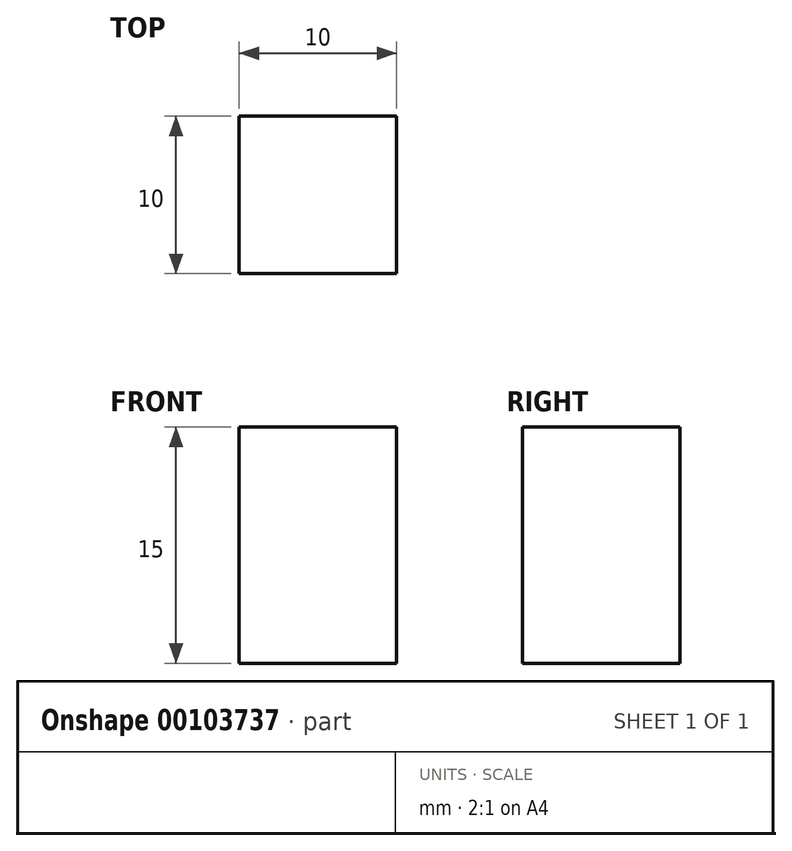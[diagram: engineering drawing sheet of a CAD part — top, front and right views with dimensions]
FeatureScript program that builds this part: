
annotation { "Feature Type Name" : "Feature", "Feature Type Description" : "" }
export const myFeature = defineFeature(function(context is Context, id is Id, definition is map)
    precondition{}
    {
        {
            var Q0;
            Q0=qCreatedBy(makeId("Top.planeOp"),FACE);
            var sketch = newSketch(context, id + "F0", { "sketchPlane" : qUnion([Q0])});
            skLineSegment(sketch, "E0.bottom", {"start": v(-0.66, 3.49) * mm, "end": v(9.34, 3.49) * mm});
            skLineSegment(sketch, "E0.top", {"start": v(-0.66, -6.51) * mm, "end": v(9.34, -6.51) * mm});
            skLineSegment(sketch, "E0.left", {"start": v(-0.66, 3.49) * mm, "end": v(-0.66, -6.51) * mm});
            skLineSegment(sketch, "E0.right", {"start": v(9.34, 3.49) * mm, "end": v(9.34, -6.51) * mm});
            skSolve(sketch);
        }
        {
            var Q0;
            Q0=makeQuery(id+"F0.imprint","IMPRINT",FACE,{"disambiguationData":[TD([[makeQuery(id+"F0.imprint","IMPRINT",EDGE,{"derivedFrom":sQuery(id+"F0.wireOp",EDGE,"E0.bottom")}),-1.0]])]});
            extrude(context, id + "F1", {"entities" : qUnion([Q0]), "depth" : 15 * mm});
        }
    });
